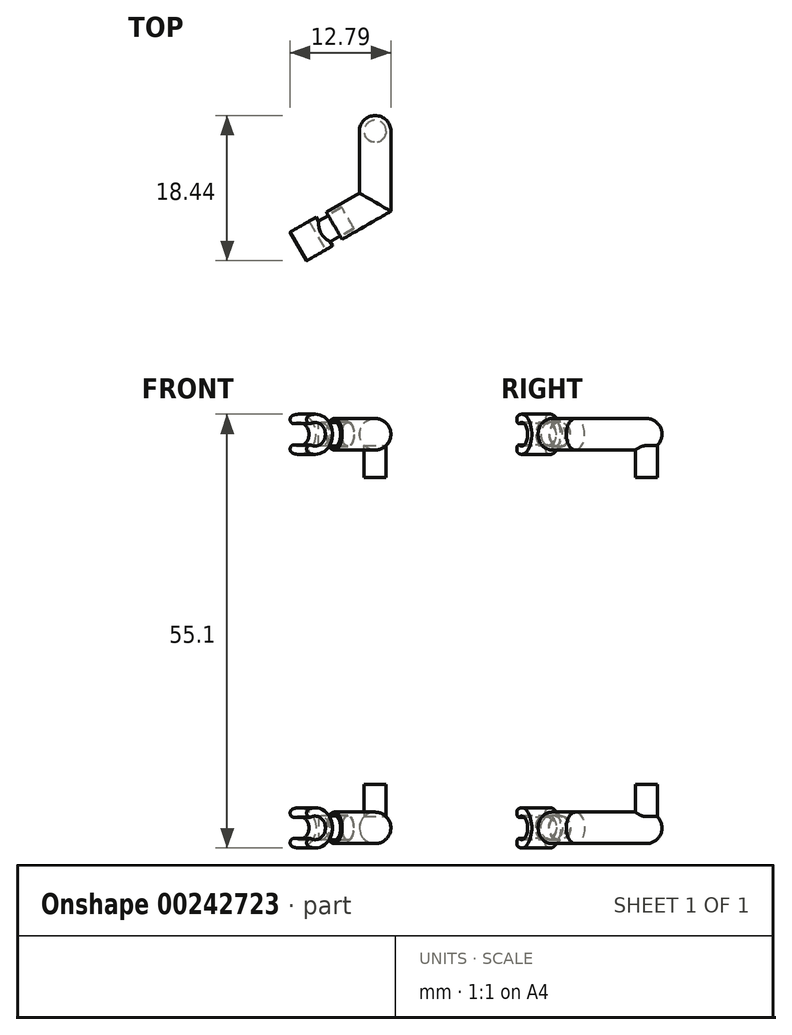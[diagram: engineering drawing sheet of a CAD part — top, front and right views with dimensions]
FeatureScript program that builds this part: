
annotation { "Feature Type Name" : "Feature", "Feature Type Description" : "" }
export const myFeature = defineFeature(function(context is Context, id is Id, definition is map)
    precondition{}
    {
        {
            var Q0;
            Q0=qCreatedBy(makeId("Top.planeOp"),FACE);
            var sketch = newSketch(context, id + "F0", { "sketchPlane" : qUnion([Q0])});
            skLineSegment(sketch, "E0", {"start": v(0, 0) * mm, "end": v(0, -9) * mm});
            skLineSegment(sketch, "E1", {"start": v(0, -9) * mm, "end": v(-5.2, -12) * mm});
            skLineSegment(sketch, "E2", {"start": v(0, 13.87) * mm, "end": v(0, -14.86) * mm, "construction": true});
            skSolve(sketch);
        }
        {
            var Q0;
            Q0=qCreatedBy(makeId("Front.planeOp"),FACE);
            var sketch = newSketch(context, id + "F1", { "sketchPlane" : qUnion([Q0])});
            skCircle(sketch, "E3", {"center": v(0, 0) * mm, "radius": 2 * mm});
            skSolve(sketch);
        }
        {
            var Q0;
            Q0=makeQuery(id+"F1.imprint","IMPRINT",FACE,{"disambiguationData":[TD([[makeQuery(id+"F1.imprint","IMPRINT",EDGE,{"derivedFrom":sQuery(id+"F1.wireOp",EDGE,"E3")}),1.0]])]});
            var Q1;
            Q1=sQuery(id+"F0.wireOp",EDGE,"E0");
            var Q2;
            Q2=sQuery(id+"F0.wireOp",EDGE,"E1");
            sweep(context, id + "F2", {"profiles" : qUnion([Q0]), "path" : qUnion([Q1, Q2])});
        }
        {
            var Q0;
            Q0=makeQuery(id+"F2.opSweep","CAP_FACE",FACE,{"disambiguationData":[OSD([sQuery(id+"F0.wireOp",VERTEX,"E0.start"),sQuery(id+"F1.wireOp",EDGE,"E3")])],"isStart":true});
            var sketch = newSketch(context, id + "F3", { "sketchPlane" : qUnion([Q0])});
            skCircle(sketch, "E4.0.0", {"center": v(0, 0) * mm, "radius": 2 * mm});
            skLineSegment(sketch, "E5", {"start": v(0, -2) * mm, "end": v(0, 2) * mm});
            skSolve(sketch);
        }
        {
            var Q0;
            {var subQ0=sQuery(id+"F3.wireOp",EDGE,"E5");Q0=makeQuery(id+"F3.imprint","IMPRINT",FACE,{"disambiguationData":[TD([[makeQuery(id+"F3.imprint","IMPRINT",EDGE,{"derivedFrom":subQ0}),1.0]])]});}
            var Q1;
            Q1=sQuery(id+"F3.wireOp",EDGE,"E5");
            revolve(context, id + "F4", {"operationType" : NewBodyOperationType.ADD, "entities" : qUnion([Q0]), "axis" : qUnion([Q1]), "revolveType" : RevolveType.FULL});
        }
        {
            var Q0;
            Q0=makeQuery(id+"F2.opSweep","CAP_FACE",FACE,{"disambiguationData":[OSD([sQuery(id+"F0.wireOp",VERTEX,"E1.end"),sQuery(id+"F1.wireOp",EDGE,"E3")])],"isStart":false});
            var sketch = newSketch(context, id + "F5", { "sketchPlane" : qUnion([Q0])});
            skCircle(sketch, "E6.0", {"center": v(7.8, 0) * mm, "radius": 1.5 * mm});
            skSolve(sketch);
        }
        {
            var Q0;
            Q0=makeQuery(id+"F5.imprint","IMPRINT",FACE,{"disambiguationData":[TD([[makeQuery(id+"F5.imprint","IMPRINT",EDGE,{"derivedFrom":sQuery(id+"F5.wireOp",EDGE,"E6.0")}),1.0]])]});
            extrude(context, id + "F6", {"entities" : qUnion([Q0]), "oppositeDirection" : true, "depth" : 2 * mm, "hasSecondDirection" : true, "secondDirectionOppositeDirection" : false, "secondDirectionDepth" : 4 * mm});
        }
        {
            var Q0;
            Q0=makeQuery(id+"F6.opExtrude","CAP_FACE",FACE,{"disambiguationData":[OSD([sQuery(id+"F5.wireOp",EDGE,"E6.0")])],"isStart":true});
            var sketch = newSketch(context, id + "F7", { "sketchPlane" : qUnion([Q0])});
            skCircle(sketch, "E7.0.0", {"center": v(7.8, 0) * mm, "radius": 1.5 * mm, "construction": true});
            skLineSegment(sketch, "E8", {"start": v(7.8, 1.5) * mm, "end": v(7.8, -1.5) * mm});
            skSolve(sketch);
        }
        {
            var Q0;
            Q0=sQuery(id+"F7.wireOp",EDGE,"E8");
            cPlane(context, id + "F8", {"entities" : qUnion([Q0]), "cplaneType" : CPlaneType.LINE_ANGLE, "offset" : 25 * mm, "angle" : 60 * degree, "width" : 150 * mm, "height" : 150 * mm});
        }
        {
            var Q0;
            Q0=qCreatedBy(id+"F8.planeOp",FACE);
            var sketch = newSketch(context, id + "F9", { "sketchPlane" : qUnion([Q0])});
            skPoint(sketch, "E9.0", {"position": v(14.5, 0) * mm});
            skCircle(sketch, "E10", {"center": v(14.5, 0) * mm, "radius": 1.5 * mm});
            skCircle(sketch, "E11", {"center": v(14.5, 0) * mm, "radius": 2.55 * mm});
            skLineSegment(sketch, "E12", {"start": v(15.75, 2.22) * mm, "end": v(15.75, -2.22) * mm});
            skSolve(sketch);
        }
        {
            var Q0;
            Q0=makeQuery(id+"F9.imprint","IMPRINT",FACE,{"disambiguationData":[TD([[makeQuery(id+"F9.imprint","IMPRINT",EDGE,{"derivedFrom":sQuery(id+"F9.wireOp",EDGE,"E10")}),-1.0]])]});
            var Q1;
            Q1=makeQuery(id+"F9.imprint","IMPRINT",FACE,{"disambiguationData":[TD([[makeQuery(id+"F9.imprint","IMPRINT",EDGE,{"derivedFrom":sQuery(id+"F9.wireOp",EDGE,"E10")}),1.0]])]});
            extrude(context, id + "F10", {"entities" : qUnion([Q0, Q1]), "operationType" : NewBodyOperationType.REMOVE, "oppositeDirection" : true, "depth" : 25 * mm, "hasSecondDirection" : true, "secondDirectionOppositeDirection" : false, "secondDirectionDepth" : 25 * mm});
        }
        {
            var Q0;
            {var subQ0=sQuery(id+"F9.wireOp",EDGE,"E12");var subQ1=sQuery(id+"F9.wireOp",EDGE,"E10");var subQ2=makeQuery(id+"F9.imprint","INTERSECT",VERTEX,{"disambiguationData":[OD(0.0)],"derivedFrom":[subQ1,subQ0]});Q0=makeQuery(id+"F9.imprint","IMPRINT",FACE,{"disambiguationData":[TD([[makeQuery(id+"F9.imprint","IMPRINT",EDGE,{"disambiguationData":[TD([[subQ2,-1.0]])],"derivedFrom":subQ1}),-1.0]])]});}
            extrude(context, id + "F11", {"entities" : qUnion([Q0]), "operationType" : NewBodyOperationType.ADD, "depth" : 2.1 * mm, "hasSecondDirection" : true, "secondDirectionOppositeDirection" : true, "secondDirectionDepth" : 2.1 * mm});
        }
        {
            var Q0;
            {var subQ0=sQuery(id+"F9.wireOp",EDGE,"E12");var subQ1=sQuery(id+"F9.wireOp",EDGE,"E10");Q0=makeQuery(id+"F11.opExtrude","SWEPT_EDGE",EDGE,{"disambiguationData":[OSD([subQ1,subQ0]),TDD([makeQuery(id+"F9.imprint","INTERSECT",VERTEX,{"disambiguationData":[OD(1.0)],"derivedFrom":[subQ1,subQ0]})])]});}
            var Q1;
            {var subQ0=sQuery(id+"F9.wireOp",EDGE,"E12");var subQ1=sQuery(id+"F9.wireOp",EDGE,"E10");Q1=makeQuery(id+"F11.opExtrude","SWEPT_EDGE",EDGE,{"disambiguationData":[OSD([subQ1,subQ0]),TDD([makeQuery(id+"F9.imprint","INTERSECT",VERTEX,{"disambiguationData":[OD(0.0)],"derivedFrom":[subQ1,subQ0]})])]});}
            var Q2;
            {var subQ0=sQuery(id+"F9.wireOp",EDGE,"E12");var subQ1=sQuery(id+"F9.wireOp",EDGE,"E11");Q2=makeQuery(id+"F11.opExtrude","SWEPT_EDGE",EDGE,{"disambiguationData":[OSD([subQ1,subQ0]),TDD([makeQuery(id+"F9.imprint","INTERSECT",VERTEX,{"disambiguationData":[OD(1.0)],"derivedFrom":[subQ1,subQ0]})])]});}
            var Q3;
            {var subQ0=sQuery(id+"F9.wireOp",EDGE,"E12");var subQ1=sQuery(id+"F9.wireOp",EDGE,"E11");Q3=makeQuery(id+"F11.opExtrude","SWEPT_EDGE",EDGE,{"disambiguationData":[OSD([subQ1,subQ0]),TDD([makeQuery(id+"F9.imprint","INTERSECT",VERTEX,{"disambiguationData":[OD(0.0)],"derivedFrom":[subQ1,subQ0]})])]});}
            fillet(context, id + "F12", {"entities" : qUnion([Q0, Q1, Q2, Q3]), "radius" : .5 * mm, "tangentPropagation" : true, "allowEdgeOverflow" : false});
        }
        {
            var Q0;
            Q0=qCreatedBy(makeId("Top.planeOp"),FACE);
            var sketch = newSketch(context, id + "F13", { "sketchPlane" : qUnion([Q0])});
            skCircle(sketch, "E13", {"center": v(0, 0) * mm, "radius": 1.4 * mm});
            skSolve(sketch);
        }
        {
            var Q0;
            Q0 = qSketchRegion(id + "F13", true);
            extrude(context, id + "F14", {"entities" : qUnion([Q0]), "operationType" : NewBodyOperationType.ADD, "depth" : 5.5 * mm});
        }
        {
            var Q0;
            Q0=qCreatedBy(makeId("Right.planeOp"),FACE);
            var sketch = newSketch(context, id + "F15", { "sketchPlane" : qUnion([Q0])});
            skLineSegment(sketch, "E14", {"start": v(-9, 2) * mm, "end": v(-1.5, 2) * mm});
            skLineSegment(sketch, "E15", {"start": v(0, -2) * mm, "end": v(-9, -2) * mm});
            skSolve(sketch);
        }
        {
            var Q0;
            Q0 = qBodyType(qCreatedBy(id + "F15" ,EDGE), BodyType.WIRE);
            cPlane(context, id + "F16", {"entities" : qUnion([Q0]), "cplaneType" : CPlaneType.LINE_ANGLE, "offset" : 25 * mm, "angle" : 90 * degree, "width" : 150 * mm, "height" : 150 * mm});
        }
        {
            var Q0;
            Q0=qCreatedBy(id+"F16.planeOp",FACE);
            cPlane(context, id + "F17", {"entities" : qUnion([Q0]), "cplaneType" : CPlaneType.OFFSET, "offset" : .20 * mm, "width" : 150 * mm, "height" : 150 * mm});
        }
        {
            var Q0;
            Q0=qCreatedBy(id+"F17.planeOp",FACE);
            var sketch = newSketch(context, id + "F18", { "sketchPlane" : qUnion([Q0])});
            skLineSegment(sketch, "E16", {"start": v(2.72, -5.98) * mm, "end": v(-1.97, -12.9) * mm});
            skSolve(sketch);
        }
        {
            var Q0;
            Q0=makeQuery(id+"F6.opExtrude","SWEPT_BODY",BODY,{"disambiguationData":[OSD([sQuery(id+"F5.wireOp",EDGE,"E6.0")])]});
            var Q1;
            Q1=makeQuery(id+"F2.opSweep","SWEPT_BODY",BODY,{"disambiguationData":[OSD([sQuery(id+"F0.wireOp",EDGE,"E1"),sQuery(id+"F1.wireOp",EDGE,"E3")])]});
            var Q2;
            Q2=makeQuery(id+"F6.opExtrude","SWEPT_FACE",FACE,{"disambiguationData":[OSD([sQuery(id+"F5.wireOp",EDGE,"E6.0")])]});
            booleanBodies(context, id + "F19", {"operationType" : BooleanOperationType.SUBTRACTION, "tools" : qUnion([Q0]), "targets" : qUnion([Q1]), "offset" : true, "entitiesToOffset" : qUnion([Q2]), "offsetDistance" : .1 * mm, "keepTools" : true});
        }
        {
            var Q0;
            Q0=qCreatedBy(makeId("Top.planeOp"),FACE);
            cPlane(context, id + "F20", {"entities" : qUnion([Q0]), "cplaneType" : CPlaneType.OFFSET, "offset" : 25 * mm, "width" : 150 * mm, "height" : 150 * mm});
        }
        {
            var Q0;
            Q0=makeQuery(id+"F2.opSweep","SWEPT_BODY",BODY,{"disambiguationData":[OSD([sQuery(id+"F0.wireOp",EDGE,"E1"),sQuery(id+"F1.wireOp",EDGE,"E3")])]});
            var Q1;
            Q1=makeQuery(id+"F6.opExtrude","SWEPT_BODY",BODY,{"disambiguationData":[OSD([sQuery(id+"F5.wireOp",EDGE,"E6.0")])]});
            var Q2;
            Q2=qCreatedBy(id+"F20.planeOp",FACE);
            mirror(context, id + "F21", {"entities" : qUnion([Q0, Q1]), "mirrorPlane" : qUnion([Q2])});
        }
    });
